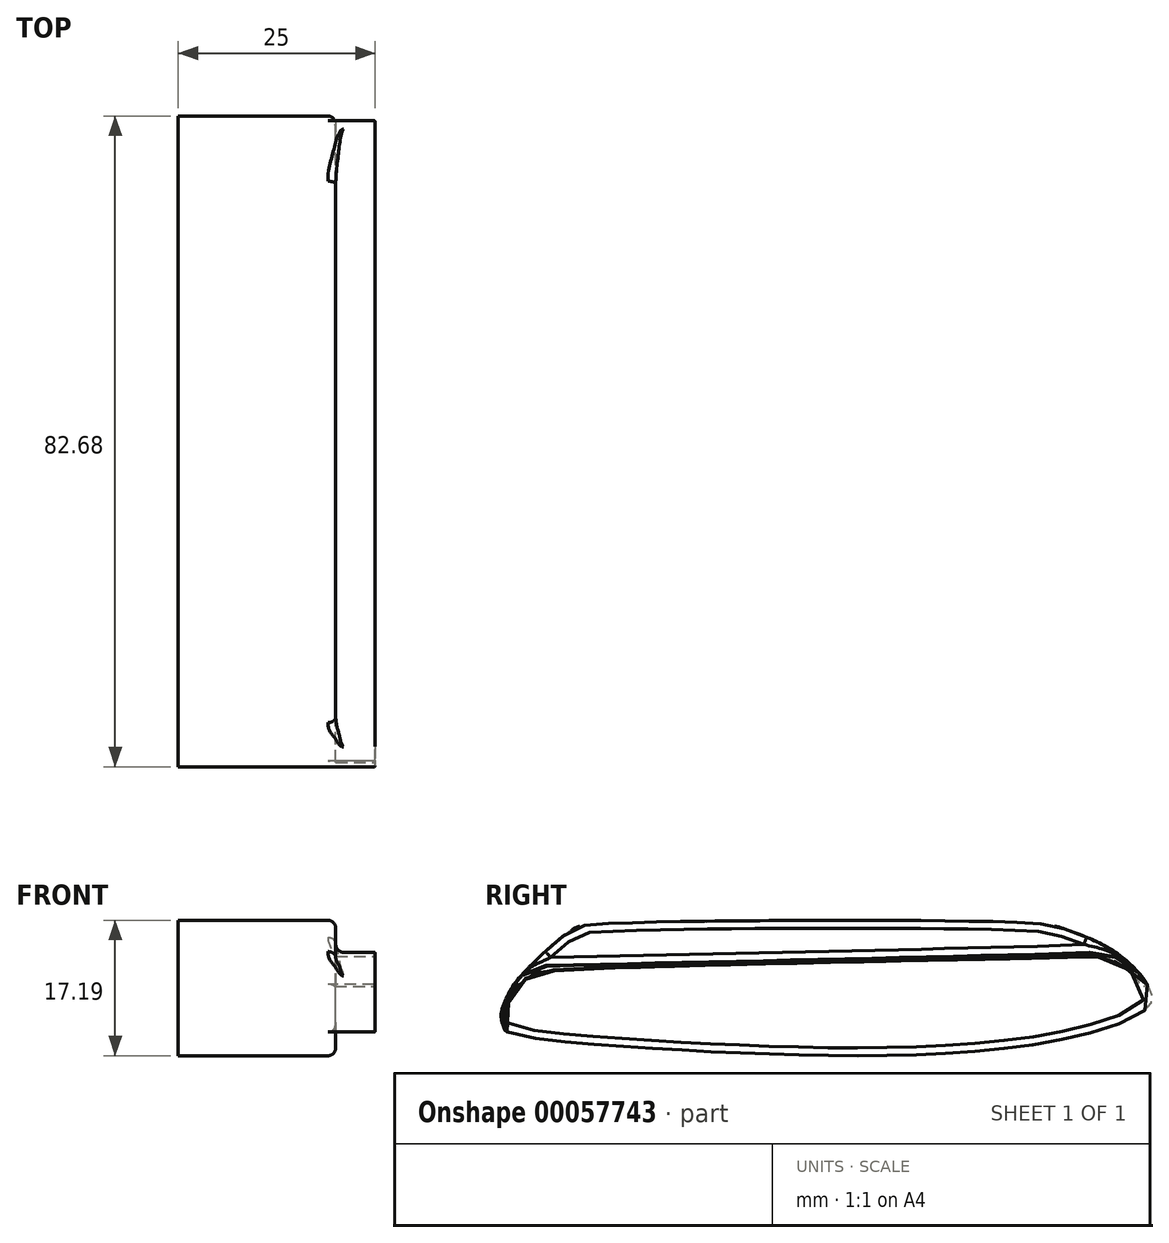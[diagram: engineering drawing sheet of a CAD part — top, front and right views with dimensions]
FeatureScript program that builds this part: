
annotation { "Feature Type Name" : "Feature", "Feature Type Description" : "" }
export const myFeature = defineFeature(function(context is Context, id is Id, definition is map)
    precondition{}
    {
        {
            var Q0;
            Q0=qCreatedBy(makeId("Right.planeOp"),FACE);
            var sketch = newSketch(context, id + "F0", { "sketchPlane" : qUnion([Q0])});
            skCircle(sketch, "E0", {"center": v(-28.96, -3.17) * mm, "radius": 5 * mm});
            skCircle(sketch, "E1", {"center": v(-2.58, -4.3) * mm, "radius": 5 * mm});
            skCircle(sketch, "E2", {"center": v(39.7, -1.22) * mm, "radius": 5 * mm});
            skCircle(sketch, "E3", {"center": v(-18.18, -4.4) * mm, "radius": 5 * mm});
            skCircle(sketch, "E4", {"center": v(-10.3, -4.22) * mm, "radius": 5 * mm});
            skCircle(sketch, "E5", {"center": v(5.45, -4.3) * mm, "radius": 5 * mm});
            skCircle(sketch, "E6", {"center": v(13.65, -4.38) * mm, "radius": 5 * mm});
            skCircle(sketch, "E7", {"center": v(21.76, -4.3) * mm, "radius": 5 * mm});
            skCircle(sketch, "E8", {"center": v(30, -3.33) * mm, "radius": 5 * mm});
            skCircle(sketch, "E9", {"center": v(-23.68, -3.72) * mm, "radius": 5 * mm});
            skFitSpline(sketch, "E10", {"points": [v(-24.17, -9.89) * mm, v(-31.03, -7.92) * mm, v(-32.53, -6.92) * mm, v(-33.27, -6.1) * mm, v(-33.97, -4.52) * mm, v(-34.12, -2.96) * mm, v(-33.94, -1.56) * mm, v(-32.9, 0.38) * mm, v(-30.87, 1.84) * mm, v(-29.21, 2.25) * mm, v(-21.63, 2.4) * mm, v(-13.26, 2.7) * mm, v(0.23, 3.13) * mm, v(12.27, 3.48) * mm, v(21.47, 3.78) * mm, v(33.09, 4.1) * mm, v(40.9, 4.3) * mm, v(43.62, 3.13) * mm, v(44.92, 1.76) * mm, v(45.6, 0.14) * mm, v(45.77, -1.5) * mm, v(45.48, -3) * mm, v(44.3, -5.04) * mm, v(42.31, -6.55) * mm, v(39.76, -7.29) * mm, v(33.79, -9.01) * mm, v(30.2, -9.88) * mm, v(27.4, -9.9) * mm, v(15.87, -9.91) * mm, v(8.9, -9.95) * mm, v(0.58, -9.94) * mm, v(-6.07, -9.92) * mm, v(-23.25, -9.9) * mm, v(-24, -9.9) * mm, v(-24.17, -9.89) * mm]});
            skFitSpline(sketch, "E11", {"points": [v(36.24, 2.39) * mm, v(-29.3, 0.64) * mm, v(-31.26, -0.5) * mm, v(-31.92, -1.76) * mm, v(-32.1, -3.51) * mm, v(-31.2, -5.66) * mm, v(-24.35, -8.14) * mm, v(-14.07, -8.25) * mm, v(26.48, -8.3) * mm, v(38.18, -5.98) * mm], "startDerivative": vector(-329.05, -3.13) * mm, "endDerivative": vector(74.4, 23.16) * mm});
            skSolve(sketch);
        }
        {
            var Q0;
            Q0=qCreatedBy(makeId("Right.planeOp"),FACE);
            var sketch = newSketch(context, id + "F1", { "sketchPlane" : qUnion([Q0])});
            skFitSpline(sketch, "E12", {"points": [v(36.5, 8.31) * mm, v(42.87, 5.28) * mm, v(46.9, 0.9) * mm, v(46.83, -1.43) * mm, v(31.26, -6.4) * mm, v(-11.57, -7.01) * mm, v(-34.69, -4.66) * mm, v(-35.08, -4.1) * mm, v(-35.44, -2.66) * mm, v(-34.57, 0) * mm, v(-32.87, 2.52) * mm, v(-27.16, 7.83) * mm, v(-23, 9.05) * mm, v(30.36, 9.25) * mm, v(36.5, 8.31) * mm]});
            skFitSpline(sketch, "E13", {"points": [v(-34.68, -4.66) * mm, v(-34.8, -3.51) * mm, v(-34.69, -1.45) * mm, v(-33.15, 1.3) * mm, v(-31.66, 2.48) * mm, v(-28.8, 3.1) * mm, v(36.47, 4.84) * mm, v(38.94, 4.94) * mm, v(41.08, 4.8) * mm, v(42.63, 4.23) * mm, v(45.1, 2.3) * mm, v(46.13, 1.12) * mm, v(46.64, 1.4) * mm], "startDerivative": vector(12.96, 14.65) * mm, "endDerivative": vector(18.3, 7.73) * mm});
            skFitSpline(sketch, "E14", {"points": [v(-32.87, 2.52) * mm, v(-31.16, 3.66) * mm, v(-28.85, 3.82) * mm, v(36.43, 5.35) * mm, v(38.82, 5.46) * mm, v(41.16, 5.35) * mm, v(42.86, 4.79) * mm, v(45.56, 2.87) * mm], "startDerivative": vector(36.83, 28.97) * mm, "endDerivative": vector(25.96, -24.19) * mm});
            skSolve(sketch);
        }
        {
            var Q0;
            {var subQ0=sQuery(id+"F1.wireOp",EDGE,"E14");Q0=makeQuery(id+"F1.imprint","IMPRINT",FACE,{"disambiguationData":[TD([[makeQuery(id+"F1.imprint","IMPRINT",EDGE,{"derivedFrom":subQ0}),1.0]])]});}
            var Q1;
            {var subQ0=sQuery(id+"F1.wireOp",EDGE,"E13");Q1=makeQuery(id+"F1.imprint","IMPRINT",FACE,{"disambiguationData":[TD([[makeQuery(id+"F1.imprint","IMPRINT",EDGE,{"derivedFrom":subQ0}),1.0]])]});}
            var Q2;
            {var subQ0=sQuery(id+"F1.wireOp",EDGE,"E13");Q2=makeQuery(id+"F1.imprint","IMPRINT",FACE,{"disambiguationData":[TD([[makeQuery(id+"F1.imprint","IMPRINT",EDGE,{"derivedFrom":subQ0}),-1.0]])]});}
            extrude(context, id + "F2", {"entities" : qUnion([Q0, Q1, Q2]), "oppositeDirection" : true, "depth" : 20 * mm});
        }
        {
            var Q0;
            {var subQ0=sQuery(id+"F1.wireOp",EDGE,"E13");Q0=makeQuery(id+"F1.imprint","IMPRINT",FACE,{"disambiguationData":[TD([[makeQuery(id+"F1.imprint","IMPRINT",EDGE,{"derivedFrom":subQ0}),1.0]])]});}
            extrude(context, id + "F3", {"entities" : qUnion([Q0]), "operationType" : NewBodyOperationType.ADD, "depth" : 5 * mm});
        }
        {
            var Q0;
            Q0=makeQuery(id+"F3.opExtrude","CAP_FACE",FACE,{"disambiguationData":[OSD([sQuery(id+"F1.wireOp",EDGE,"E12"),sQuery(id+"F1.wireOp",EDGE,"E13"),sQuery(id+"F1.wireOp",EDGE,"E14")])],"isStart":false});
            fillet(context, id + "F4", {"entities" : qUnion([Q0]), "radius" : .1 * mm, "tangentPropagation" : true, "allowEdgeOverflow" : false});
        }
        {
            var Q0;
            Q0=makeQuery(id+"F3.opExtrude","CAP_EDGE",EDGE,{"disambiguationData":[OSD([sQuery(id+"F1.wireOp",EDGE,"E14")])],"isStart":true});
            fillet(context, id + "F5", {"entities" : qUnion([Q0]), "radius" : 1 * mm, "tangentPropagation" : true, "allowEdgeOverflow" : false});
        }
        {
            var Q0;
            {var subQ1=sQuery(id+"F1.wireOp",EDGE,"E12");var subQ2=sQuery(id+"F1.wireOp",EDGE,"E14");Q0=makeQuery(id+"F3.boolean.opBoolean","SPLIT",EDGE,{"disambiguationData":[TD([makeQuery(id+"F3.opExtrude","SWEPT_FACE",FACE,{"disambiguationData":[OSD([subQ2])]})])],"derivedFrom":makeQuery(id+"F2.opExtrude","CAP_EDGE",EDGE,{"disambiguationData":[OSD([subQ1])],"isStart":true})});}
            fillet(context, id + "F6", {"entities" : qUnion([Q0]), "radius" : 1 * mm, "tangentPropagation" : true, "allowEdgeOverflow" : false});
        }
    });
